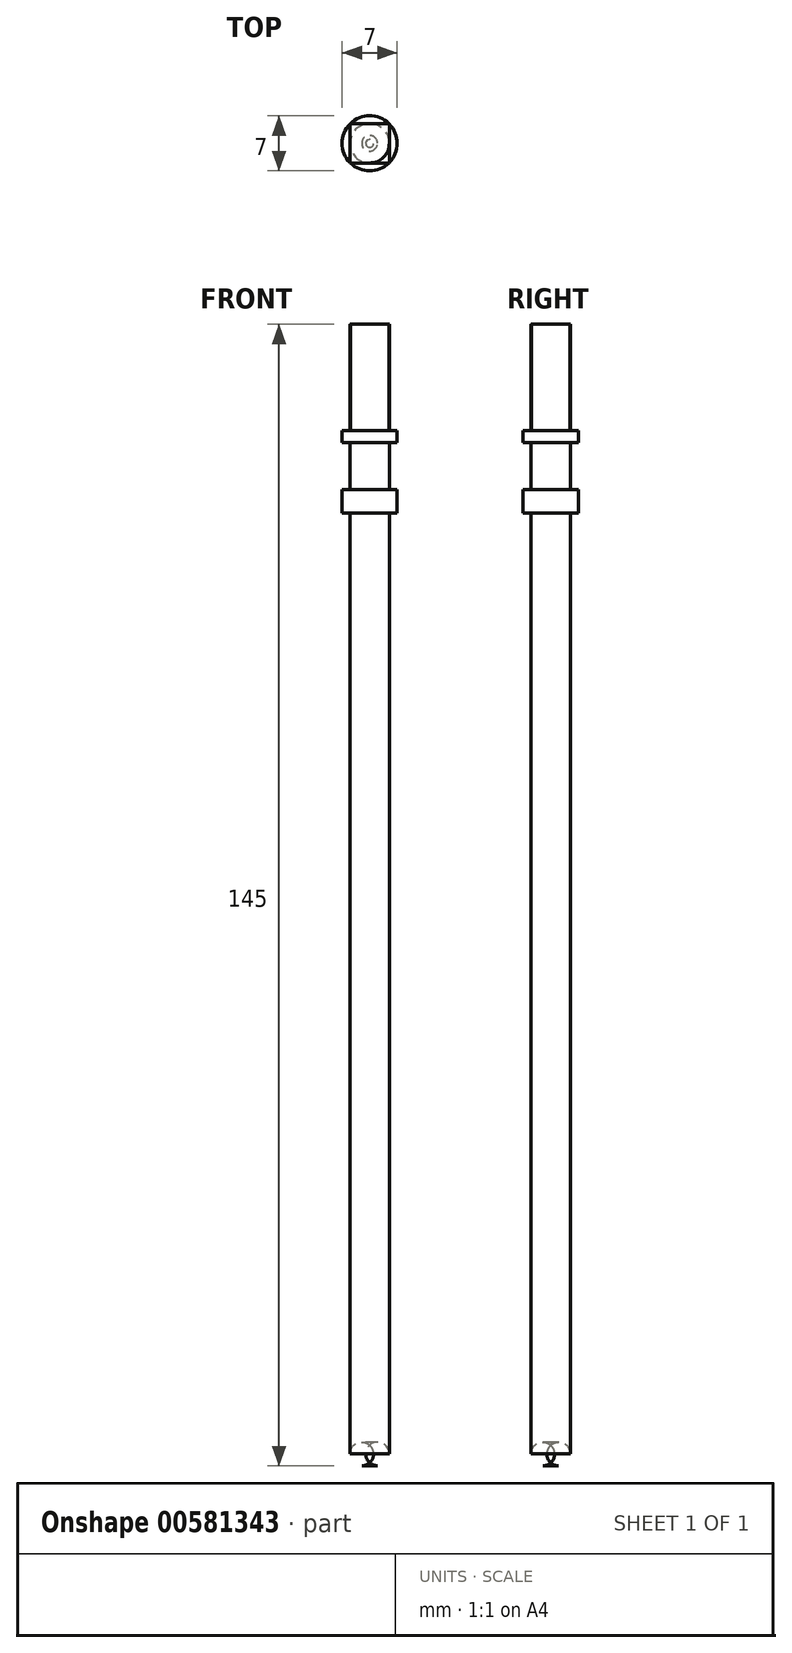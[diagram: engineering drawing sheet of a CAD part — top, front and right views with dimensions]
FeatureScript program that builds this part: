
annotation { "Feature Type Name" : "Feature", "Feature Type Description" : "" }
export const myFeature = defineFeature(function(context is Context, id is Id, definition is map)
    precondition{}
    {
        {
            var Q0;
            Q0=qCreatedBy(makeId("Top.planeOp"),FACE);
            var sketch = newSketch(context, id + "F0", { "sketchPlane" : qUnion([Q0])});
            skCircle(sketch, "E0", {"center": v(0, 0) * mm, "radius": 2.5 * mm});
            skSolve(sketch);
        }
        {
            var Q0;
            Q0=makeQuery(id+"F0.imprint","IMPRINT",FACE,{"disambiguationData":[TD([[makeQuery(id+"F0.imprint","IMPRINT",EDGE,{"derivedFrom":sQuery(id+"F0.wireOp",EDGE,"E0")}),1.0]])]});
            extrude(context, id + "F1", {"entities" : qUnion([Q0]), "endBound" : BoundingType.SYMMETRIC, "depth" : 130 * mm, "offsetDistance" : 25 * mm});
        }
        {
            var Q0;
            Q0=makeQuery(id+"F1.opExtrude","CAP_FACE",FACE,{"disambiguationData":[OSD([sQuery(id+"F0.wireOp",EDGE,"E0")])],"isStart":true});
            fillet(context, id + "F2", {"entities" : qUnion([Q0]), "radius" : 1.5 * mm, "tangentPropagation" : true, "allowEdgeOverflow" : false});
        }
        {
            var Q0;
            Q0=makeQuery(id+"F1.opExtrude","CAP_FACE",FACE,{"disambiguationData":[OSD([sQuery(id+"F0.wireOp",EDGE,"E0")])],"isStart":false});
            var sketch = newSketch(context, id + "F3", { "sketchPlane" : qUnion([Q0])});
            skLineSegment(sketch, "E1.bottom", {"start": v(2.5, -2.5) * mm, "end": v(-2.5, -2.5) * mm});
            skLineSegment(sketch, "E1.top", {"start": v(2.5, 2.5) * mm, "end": v(-2.5, 2.5) * mm});
            skLineSegment(sketch, "E1.left", {"start": v(2.5, -2.5) * mm, "end": v(2.5, 2.5) * mm});
            skLineSegment(sketch, "E1.right", {"start": v(-2.5, -2.5) * mm, "end": v(-2.5, 2.5) * mm});
            skPoint(sketch, "E1.middle", {"position": v(0, 0) * mm});
            skCircle(sketch, "E2", {"center": v(0, 0) * mm, "radius": 3.5 * mm});
            skSolve(sketch);
        }
        {
            var Q0;
            {var subQ0=makeQuery(id+"F1.opExtrude","CAP_EDGE",EDGE,{"disambiguationData":[OSD([sQuery(id+"F0.wireOp",EDGE,"E0")])],"isStart":false});var subQ1=makeQuery(id+"F3.imprint","INTERSECT",VERTEX,{"derivedFrom":[subQ0,sQuery(id+"F3.wireOp",EDGE,"E1.bottom")]});Q0=makeQuery(id+"F3.imprint","IMPRINT",FACE,{"disambiguationData":[TD([[makeQuery(id+"F3.imprint","IMPRINT",EDGE,{"disambiguationData":[TD([[subQ1,-1.0]])],"derivedFrom":subQ0}),1.0]])]});}
            var Q1;
            {var subQ0=sQuery(id+"F3.wireOp",EDGE,"E2");var subQ1=sQuery(id+"F3.wireOp",EDGE,"E1.bottom");var subQ2=makeQuery(id+"F3.imprint","INTERSECT",VERTEX,{"disambiguationData":[OD(1.0)],"derivedFrom":[subQ1,subQ0]});Q1=makeQuery(id+"F3.imprint","IMPRINT",FACE,{"disambiguationData":[TD([[makeQuery(id+"F3.imprint","IMPRINT",EDGE,{"disambiguationData":[TD([[subQ2,1.0]])],"derivedFrom":subQ1}),-1.0]])]});}
            var Q2;
            {var subQ0=sQuery(id+"F3.wireOp",EDGE,"E2");var subQ1=sQuery(id+"F3.wireOp",EDGE,"E1.bottom");var subQ2=makeQuery(id+"F3.imprint","INTERSECT",VERTEX,{"disambiguationData":[OD(0.0)],"derivedFrom":[subQ1,subQ0]});Q2=makeQuery(id+"F3.imprint","IMPRINT",FACE,{"disambiguationData":[TD([[makeQuery(id+"F3.imprint","IMPRINT",EDGE,{"disambiguationData":[TD([[subQ2,-1.0]])],"derivedFrom":subQ1}),-1.0]])]});}
            var Q3;
            {var subQ0=sQuery(id+"F3.wireOp",EDGE,"E2");var subQ1=sQuery(id+"F3.wireOp",EDGE,"E1.top");var subQ2=makeQuery(id+"F3.imprint","INTERSECT",VERTEX,{"disambiguationData":[OD(0.0)],"derivedFrom":[subQ1,subQ0]});Q3=makeQuery(id+"F3.imprint","IMPRINT",FACE,{"disambiguationData":[TD([[makeQuery(id+"F3.imprint","IMPRINT",EDGE,{"disambiguationData":[TD([[subQ2,-1.0]])],"derivedFrom":subQ1}),1.0]])]});}
            var Q4;
            {var subQ0=sQuery(id+"F3.wireOp",EDGE,"E2");var subQ1=sQuery(id+"F3.wireOp",EDGE,"E1.top");var subQ2=makeQuery(id+"F3.imprint","INTERSECT",VERTEX,{"disambiguationData":[OD(1.0)],"derivedFrom":[subQ1,subQ0]});Q4=makeQuery(id+"F3.imprint","IMPRINT",FACE,{"disambiguationData":[TD([[makeQuery(id+"F3.imprint","IMPRINT",EDGE,{"disambiguationData":[TD([[subQ2,1.0]])],"derivedFrom":subQ1}),1.0]])]});}
            extrude(context, id + "F4", {"entities" : qUnion([Q0, Q1, Q2, Q3, Q4]), "operationType" : NewBodyOperationType.ADD, "depth" : 15 * mm, "offsetDistance" : 25 * mm});
        }
        {
            var Q0;
            {var subQ0=sQuery(id+"F3.wireOp",EDGE,"E2");var subQ1=sQuery(id+"F3.wireOp",EDGE,"E1.bottom");var subQ2=makeQuery(id+"F3.imprint","INTERSECT",VERTEX,{"disambiguationData":[OD(0.0)],"derivedFrom":[subQ1,subQ0]});Q0=makeQuery(id+"F3.imprint","IMPRINT",FACE,{"disambiguationData":[TD([[makeQuery(id+"F3.imprint","IMPRINT",EDGE,{"disambiguationData":[TD([[subQ2,-1.0]])],"derivedFrom":subQ1}),1.0]])]});}
            var Q1;
            {var subQ0=sQuery(id+"F3.wireOp",EDGE,"E2");var subQ1=sQuery(id+"F3.wireOp",EDGE,"E1.top");var subQ2=makeQuery(id+"F3.imprint","INTERSECT",VERTEX,{"disambiguationData":[OD(0.0)],"derivedFrom":[subQ1,subQ0]});Q1=makeQuery(id+"F3.imprint","IMPRINT",FACE,{"disambiguationData":[TD([[makeQuery(id+"F3.imprint","IMPRINT",EDGE,{"disambiguationData":[TD([[subQ2,-1.0]])],"derivedFrom":subQ1}),-1.0]])]});}
            var Q2;
            {var subQ0=sQuery(id+"F3.wireOp",EDGE,"E2");var subQ1=sQuery(id+"F3.wireOp",EDGE,"E1.left");var subQ2=makeQuery(id+"F3.imprint","INTERSECT",VERTEX,{"disambiguationData":[OD(0.0)],"derivedFrom":[subQ1,subQ0]});Q2=makeQuery(id+"F3.imprint","IMPRINT",FACE,{"disambiguationData":[TD([[makeQuery(id+"F3.imprint","IMPRINT",EDGE,{"disambiguationData":[TD([[subQ2,-1.0]])],"derivedFrom":subQ1}),-1.0]])]});}
            var Q3;
            {var subQ0=sQuery(id+"F3.wireOp",EDGE,"E2");var subQ1=sQuery(id+"F3.wireOp",EDGE,"E1.right");var subQ2=makeQuery(id+"F3.imprint","INTERSECT",VERTEX,{"disambiguationData":[OD(0.0)],"derivedFrom":[subQ1,subQ0]});Q3=makeQuery(id+"F3.imprint","IMPRINT",FACE,{"disambiguationData":[TD([[makeQuery(id+"F3.imprint","IMPRINT",EDGE,{"disambiguationData":[TD([[subQ2,-1.0]])],"derivedFrom":subQ1}),1.0]])]});}
            var Q4;
            {var subQ0=sQuery(id+"F3.wireOp",EDGE,"E2");var subQ1=sQuery(id+"F3.wireOp",EDGE,"E1.bottom");var subQ2=makeQuery(id+"F3.imprint","INTERSECT",VERTEX,{"disambiguationData":[OD(0.0)],"derivedFrom":[subQ1,subQ0]});Q4=makeQuery(id+"F3.imprint","IMPRINT",FACE,{"disambiguationData":[TD([[makeQuery(id+"F3.imprint","IMPRINT",EDGE,{"disambiguationData":[TD([[subQ2,-1.0]])],"derivedFrom":subQ1}),-1.0]])]});}
            var Q5;
            {var subQ0=sQuery(id+"F3.wireOp",EDGE,"E2");var subQ1=sQuery(id+"F3.wireOp",EDGE,"E1.bottom");var subQ2=makeQuery(id+"F3.imprint","INTERSECT",VERTEX,{"disambiguationData":[OD(1.0)],"derivedFrom":[subQ1,subQ0]});Q5=makeQuery(id+"F3.imprint","IMPRINT",FACE,{"disambiguationData":[TD([[makeQuery(id+"F3.imprint","IMPRINT",EDGE,{"disambiguationData":[TD([[subQ2,1.0]])],"derivedFrom":subQ1}),-1.0]])]});}
            var Q6;
            {var subQ0=sQuery(id+"F3.wireOp",EDGE,"E2");var subQ1=sQuery(id+"F3.wireOp",EDGE,"E1.top");var subQ2=makeQuery(id+"F3.imprint","INTERSECT",VERTEX,{"disambiguationData":[OD(0.0)],"derivedFrom":[subQ1,subQ0]});Q6=makeQuery(id+"F3.imprint","IMPRINT",FACE,{"disambiguationData":[TD([[makeQuery(id+"F3.imprint","IMPRINT",EDGE,{"disambiguationData":[TD([[subQ2,-1.0]])],"derivedFrom":subQ1}),1.0]])]});}
            var Q7;
            {var subQ0=sQuery(id+"F3.wireOp",EDGE,"E2");var subQ1=sQuery(id+"F3.wireOp",EDGE,"E1.top");var subQ2=makeQuery(id+"F3.imprint","INTERSECT",VERTEX,{"disambiguationData":[OD(1.0)],"derivedFrom":[subQ1,subQ0]});Q7=makeQuery(id+"F3.imprint","IMPRINT",FACE,{"disambiguationData":[TD([[makeQuery(id+"F3.imprint","IMPRINT",EDGE,{"disambiguationData":[TD([[subQ2,1.0]])],"derivedFrom":subQ1}),1.0]])]});}
            var Q8;
            {var subQ0=makeQuery(id+"F1.opExtrude","CAP_EDGE",EDGE,{"disambiguationData":[OSD([sQuery(id+"F0.wireOp",EDGE,"E0")])],"isStart":false});var subQ1=makeQuery(id+"F3.imprint","INTERSECT",VERTEX,{"derivedFrom":[subQ0,sQuery(id+"F3.wireOp",EDGE,"E1.bottom")]});Q8=makeQuery(id+"F3.imprint","IMPRINT",FACE,{"disambiguationData":[TD([[makeQuery(id+"F3.imprint","IMPRINT",EDGE,{"disambiguationData":[TD([[subQ1,-1.0]])],"derivedFrom":subQ0}),1.0]])]});}
            extrude(context, id + "F5", {"entities" : qUnion([Q0, Q1, Q2, Q3, Q4, Q5, Q6, Q7, Q8]), "operationType" : NewBodyOperationType.ADD, "depth" : -9 * mm, "offsetDistance" : 25 * mm});
        }
        {
            var Q0;
            {var subQ0=sQuery(id+"F3.wireOp",EDGE,"E2");var subQ1=sQuery(id+"F3.wireOp",EDGE,"E1.right");var subQ2=makeQuery(id+"F3.imprint","INTERSECT",VERTEX,{"disambiguationData":[OD(0.0)],"derivedFrom":[subQ1,subQ0]});Q0=makeQuery(id+"F3.imprint","IMPRINT",FACE,{"disambiguationData":[TD([[makeQuery(id+"F3.imprint","IMPRINT",EDGE,{"disambiguationData":[TD([[subQ2,-1.0]])],"derivedFrom":subQ1}),1.0]])]});}
            var Q1;
            {var subQ0=sQuery(id+"F3.wireOp",EDGE,"E2");var subQ1=sQuery(id+"F3.wireOp",EDGE,"E1.bottom");var subQ2=makeQuery(id+"F3.imprint","INTERSECT",VERTEX,{"disambiguationData":[OD(1.0)],"derivedFrom":[subQ1,subQ0]});Q1=makeQuery(id+"F3.imprint","IMPRINT",FACE,{"disambiguationData":[TD([[makeQuery(id+"F3.imprint","IMPRINT",EDGE,{"disambiguationData":[TD([[subQ2,1.0]])],"derivedFrom":subQ1}),-1.0]])]});}
            var Q2;
            {var subQ0=sQuery(id+"F3.wireOp",EDGE,"E2");var subQ1=sQuery(id+"F3.wireOp",EDGE,"E1.bottom");var subQ2=makeQuery(id+"F3.imprint","INTERSECT",VERTEX,{"disambiguationData":[OD(0.0)],"derivedFrom":[subQ1,subQ0]});Q2=makeQuery(id+"F3.imprint","IMPRINT",FACE,{"disambiguationData":[TD([[makeQuery(id+"F3.imprint","IMPRINT",EDGE,{"disambiguationData":[TD([[subQ2,-1.0]])],"derivedFrom":subQ1}),1.0]])]});}
            var Q3;
            {var subQ0=sQuery(id+"F3.wireOp",EDGE,"E2");var subQ1=sQuery(id+"F3.wireOp",EDGE,"E1.bottom");var subQ2=makeQuery(id+"F3.imprint","INTERSECT",VERTEX,{"disambiguationData":[OD(0.0)],"derivedFrom":[subQ1,subQ0]});Q3=makeQuery(id+"F3.imprint","IMPRINT",FACE,{"disambiguationData":[TD([[makeQuery(id+"F3.imprint","IMPRINT",EDGE,{"disambiguationData":[TD([[subQ2,-1.0]])],"derivedFrom":subQ1}),-1.0]])]});}
            var Q4;
            {var subQ0=sQuery(id+"F3.wireOp",EDGE,"E2");var subQ1=sQuery(id+"F3.wireOp",EDGE,"E1.left");var subQ2=makeQuery(id+"F3.imprint","INTERSECT",VERTEX,{"disambiguationData":[OD(0.0)],"derivedFrom":[subQ1,subQ0]});Q4=makeQuery(id+"F3.imprint","IMPRINT",FACE,{"disambiguationData":[TD([[makeQuery(id+"F3.imprint","IMPRINT",EDGE,{"disambiguationData":[TD([[subQ2,-1.0]])],"derivedFrom":subQ1}),-1.0]])]});}
            var Q5;
            {var subQ0=sQuery(id+"F3.wireOp",EDGE,"E2");var subQ1=sQuery(id+"F3.wireOp",EDGE,"E1.top");var subQ2=makeQuery(id+"F3.imprint","INTERSECT",VERTEX,{"disambiguationData":[OD(1.0)],"derivedFrom":[subQ1,subQ0]});Q5=makeQuery(id+"F3.imprint","IMPRINT",FACE,{"disambiguationData":[TD([[makeQuery(id+"F3.imprint","IMPRINT",EDGE,{"disambiguationData":[TD([[subQ2,1.0]])],"derivedFrom":subQ1}),1.0]])]});}
            var Q6;
            {var subQ0=sQuery(id+"F3.wireOp",EDGE,"E2");var subQ1=sQuery(id+"F3.wireOp",EDGE,"E1.top");var subQ2=makeQuery(id+"F3.imprint","INTERSECT",VERTEX,{"disambiguationData":[OD(0.0)],"derivedFrom":[subQ1,subQ0]});Q6=makeQuery(id+"F3.imprint","IMPRINT",FACE,{"disambiguationData":[TD([[makeQuery(id+"F3.imprint","IMPRINT",EDGE,{"disambiguationData":[TD([[subQ2,-1.0]])],"derivedFrom":subQ1}),-1.0]])]});}
            var Q7;
            {var subQ0=sQuery(id+"F3.wireOp",EDGE,"E2");var subQ1=sQuery(id+"F3.wireOp",EDGE,"E1.top");var subQ2=makeQuery(id+"F3.imprint","INTERSECT",VERTEX,{"disambiguationData":[OD(0.0)],"derivedFrom":[subQ1,subQ0]});Q7=makeQuery(id+"F3.imprint","IMPRINT",FACE,{"disambiguationData":[TD([[makeQuery(id+"F3.imprint","IMPRINT",EDGE,{"disambiguationData":[TD([[subQ2,-1.0]])],"derivedFrom":subQ1}),1.0]])]});}
            extrude(context, id + "F6", {"entities" : qUnion([Q0, Q1, Q2, Q3, Q4, Q5, Q6, Q7]), "operationType" : NewBodyOperationType.REMOVE, "oppositeDirection" : true, "depth" : 6 * mm, "offsetDistance" : 25 * mm});
        }
        {
            var Q0;
            {var subQ0=sQuery(id+"F3.wireOp",EDGE,"E2");var subQ1=sQuery(id+"F3.wireOp",EDGE,"E1.bottom");var subQ2=makeQuery(id+"F3.imprint","INTERSECT",VERTEX,{"disambiguationData":[OD(0.0)],"derivedFrom":[subQ1,subQ0]});Q0=makeQuery(id+"F3.imprint","IMPRINT",FACE,{"disambiguationData":[TD([[makeQuery(id+"F3.imprint","IMPRINT",EDGE,{"disambiguationData":[TD([[subQ2,-1.0]])],"derivedFrom":subQ1}),1.0]])]});}
            var Q1;
            {var subQ0=sQuery(id+"F3.wireOp",EDGE,"E2");var subQ1=sQuery(id+"F3.wireOp",EDGE,"E1.left");var subQ2=makeQuery(id+"F3.imprint","INTERSECT",VERTEX,{"disambiguationData":[OD(0.0)],"derivedFrom":[subQ1,subQ0]});Q1=makeQuery(id+"F3.imprint","IMPRINT",FACE,{"disambiguationData":[TD([[makeQuery(id+"F3.imprint","IMPRINT",EDGE,{"disambiguationData":[TD([[subQ2,-1.0]])],"derivedFrom":subQ1}),-1.0]])]});}
            var Q2;
            {var subQ0=sQuery(id+"F3.wireOp",EDGE,"E2");var subQ1=sQuery(id+"F3.wireOp",EDGE,"E1.top");var subQ2=makeQuery(id+"F3.imprint","INTERSECT",VERTEX,{"disambiguationData":[OD(0.0)],"derivedFrom":[subQ1,subQ0]});Q2=makeQuery(id+"F3.imprint","IMPRINT",FACE,{"disambiguationData":[TD([[makeQuery(id+"F3.imprint","IMPRINT",EDGE,{"disambiguationData":[TD([[subQ2,-1.0]])],"derivedFrom":subQ1}),-1.0]])]});}
            var Q3;
            {var subQ0=sQuery(id+"F3.wireOp",EDGE,"E2");var subQ1=sQuery(id+"F3.wireOp",EDGE,"E1.right");var subQ2=makeQuery(id+"F3.imprint","INTERSECT",VERTEX,{"disambiguationData":[OD(0.0)],"derivedFrom":[subQ1,subQ0]});Q3=makeQuery(id+"F3.imprint","IMPRINT",FACE,{"disambiguationData":[TD([[makeQuery(id+"F3.imprint","IMPRINT",EDGE,{"disambiguationData":[TD([[subQ2,-1.0]])],"derivedFrom":subQ1}),1.0]])]});}
            extrude(context, id + "F7", {"entities" : qUnion([Q0, Q1, Q2, Q3]), "operationType" : NewBodyOperationType.ADD, "depth" : 1.5 * mm, "offsetDistance" : 25 * mm});
        }
    });
